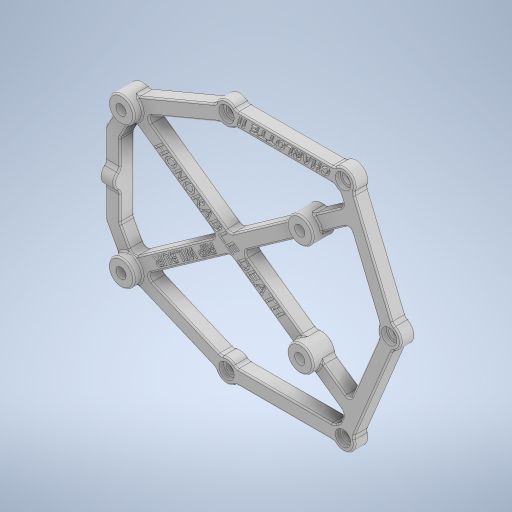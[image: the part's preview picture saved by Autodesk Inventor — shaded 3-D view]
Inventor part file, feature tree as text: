
AUTODESK INVENTOR PART (.ipt)
format: ipt  version: 2024.2 (Build 282272000, 272)  size: 1,641,984 bytes
history: native  units: mm
features: sketch x12, reference x8, extrude x7, fillet x4, hole x3, emboss x3, other x3, projected_geometry x1
ambient origin geometry x8: Origin, YZ Plane, XZ Plane, XY Plane, X Axis, Y Axis, Z Axis, Center Point
bodies: Solid1 (feature_tree)
feature tree (41):
  extrude  "Extrusion1"  Depth=9.0mm
  extrude  "Extrusion2"  Depth=5.25mm
  extrude  "Extrusion3"  Depth=49.0mm
  extrude  "Extrusion4"  Depth=5.0mm
  hole  "Hole1"  [1 undecoded]
  hole  "Hole3"  [1 undecoded]
  fillet  "Fillet1"  Radius=2.5mm
  fillet  "Fillet2"  Radius=2.5mm
  sketch  "Sketch7"  dims[d10=5.0mm d11=5.0mm d12=2.5mm d13=2.5mm]
  extrude  "Extrusion5"  Depth=2.5mm
  fillet  "Fillet3"  Radius=2.5mm
  hole  "Hole2"  [1 undecoded]
  fillet  "Fillet4"  Radius=5.0mm
  emboss  "Emboss1"
  emboss  "Emboss2"
  emboss  "Emboss3"
  extrude  "Extrusion6"  Depth=5.0mm TaperAngle=0.0deg
  extrude  "Extrusion7"  Depth=2.0mm
  sketch  "Sketch1"  dims[d0=8.0mm d1=9.0mm]
  reference  "Reference1"
  reference  "Reference2"
  reference  "Reference3"
  reference  "Reference4"
  reference  "Reference5"
  reference  "Reference6"
  reference  "Reference7"
  reference  "Reference8"
  sketch  "Sketch3"  dims[d2=5.25mm d3=5.25mm]
  projected_geometry  "Projected Loop1"
  sketch  "Sketch4"  dims[d4=62.0mm d5=49.0mm]
  sketch  "Sketch5"  dims[d6=28.0mm d7=5.0mm]
  sketch  "Sketch6"  dims[d8=2.5mm d9=2.5mm]
  sketch  "Sketch9"  dims[d14=5.0mm d15=2.5mm d16=2.5mm]
  sketch  "Sketch10"  dims[d17=5.0mm d18=5.6mm d19=5.0mm d20=0.0mm]
  sketch  "Sketch11"  dims[d21=1.9mm d22=0.0mm d23=5.0mm d24=0.0mm]
  sketch  "Sketch12"  dims[d25=3.0mm d26=0.0mm]
  sketch  "Sketch13"  dims[d27=3.5mm d28=6.0mm d29=4.0mm d30=2.0mm d31=90.0deg d32=2.0mm d33=0.0mm d34=2.0mm]
  sketch  "Sketch14"  dims[d35=1.5mm d36=7.0mm d37=3.0mm d38=0.0mm d39=2.0mm d40=2.8mm d41=6.0mm d42=4.0mm d43=2.0mm d44=90.0deg d45=4.0mm d46=0.0mm d47=0.5mm d48=0.5mm d49=0.0mm d50=5.25mm d51=6.0mm d52=4.0mm d53=2.0mm d54=90.0deg d55=1.6mm d56=0.0mm d57=1.0mm d58=0.0mm d59=0.5mm d60=0.0mm d61=2.5mm d62=2.5mm d63=5.0mm d64=2.5mm d65=2.5mm d66=5.0mm d67=0.2mm d68=0.0mm d69=0.2mm d70=0.0mm]
  other  "<userpath>\Desktop\scioly-robot-tour\Hardware\ipt\v4\v4assembly.iam"
  other  "v4assembly.iam"
  other  "v4chassisv2:1"
note: 3 required parameter values undecoded (feature->parameter linkage not recoverable at this tier; creation-order binding heuristic only, values carry confidence <= 0.55)
